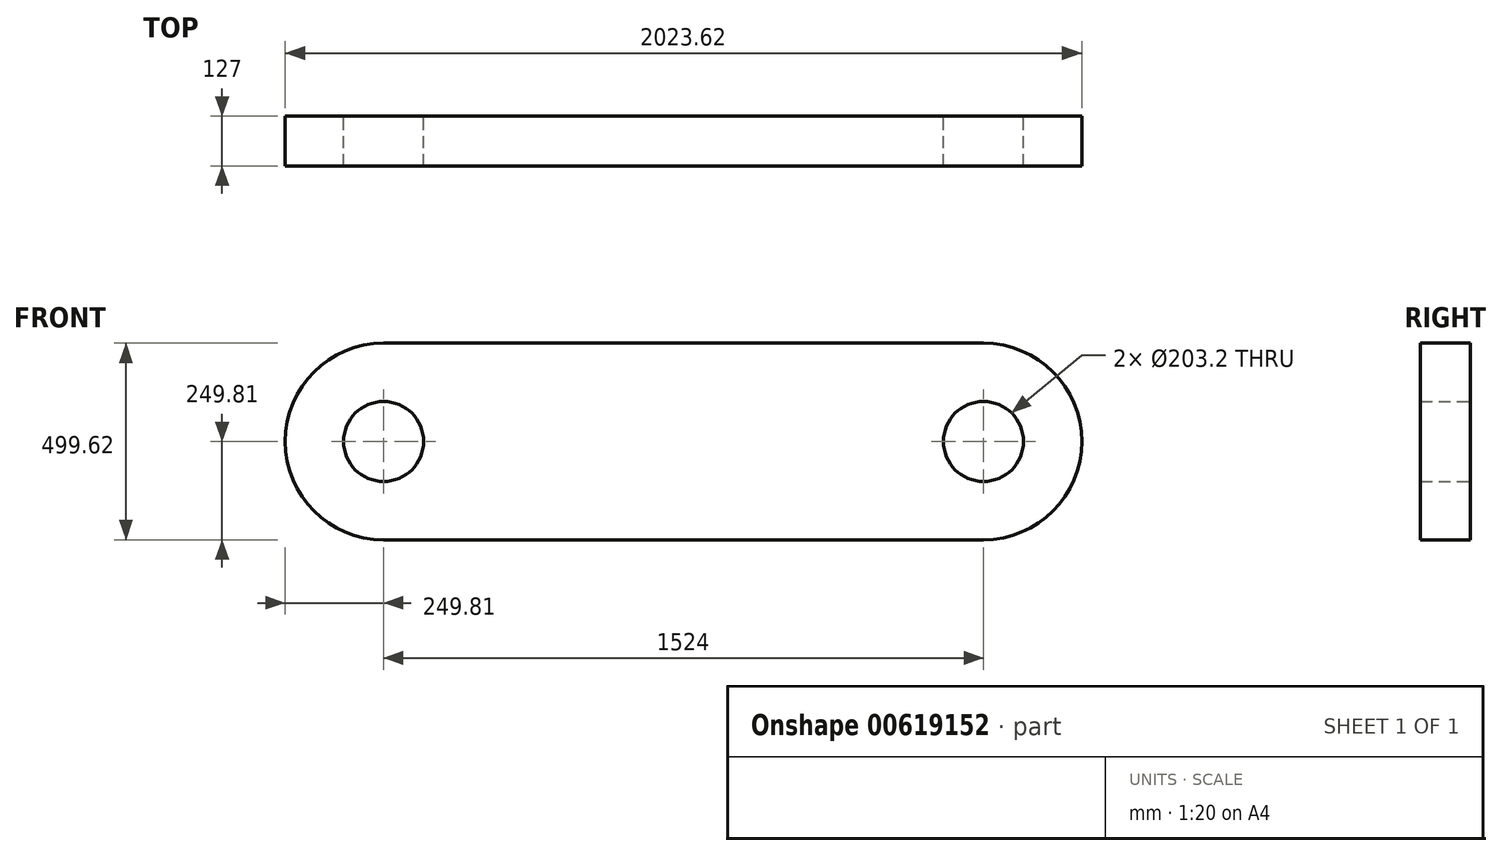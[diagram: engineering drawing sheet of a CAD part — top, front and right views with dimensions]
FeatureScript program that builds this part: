
annotation { "Feature Type Name" : "Feature", "Feature Type Description" : "" }
export const myFeature = defineFeature(function(context is Context, id is Id, definition is map)
    precondition{}
    {
        {
            var Q0;
            Q0=qCreatedBy(makeId("Front.planeOp"),FACE);
            var sketch = newSketch(context, id + "F0", { "sketchPlane" : qUnion([Q0])});
            skArc(sketch, "E0", {"start": v(0, -249.8) * mm, "mid": v(249.8, 0) * mm, "end": v(0, 249.8) * mm});
            skArc(sketch, "E1", {"start": v(-1524, 249.8) * mm, "mid": v(-1773.8, 0) * mm, "end": v(-1524, -249.8) * mm});
            skLineSegment(sketch, "E2", {"start": v(-1524, 249.8) * mm, "end": v(0, 249.8) * mm});
            skLineSegment(sketch, "E3", {"start": v(-1524, -249.8) * mm, "end": v(0, -249.8) * mm});
            skCircle(sketch, "E4", {"center": v(-1524, 0) * mm, "radius": 101.6 * mm});
            skCircle(sketch, "E5", {"center": v(0, 0) * mm, "radius": 101.6 * mm});
            skSolve(sketch);
        }
        {
            var Q0;
            Q0=makeQuery(id+"F0.imprint","IMPRINT",FACE,{"disambiguationData":[TD([[makeQuery(id+"F0.imprint","IMPRINT",EDGE,{"derivedFrom":sQuery(id+"F0.wireOp",EDGE,"E0")}),1.0]])]});
            extrude(context, id + "F1", {"entities" : qUnion([Q0]), "depth" : 127 * mm, "offsetDistance" : 25.4 * mm});
        }
    });
